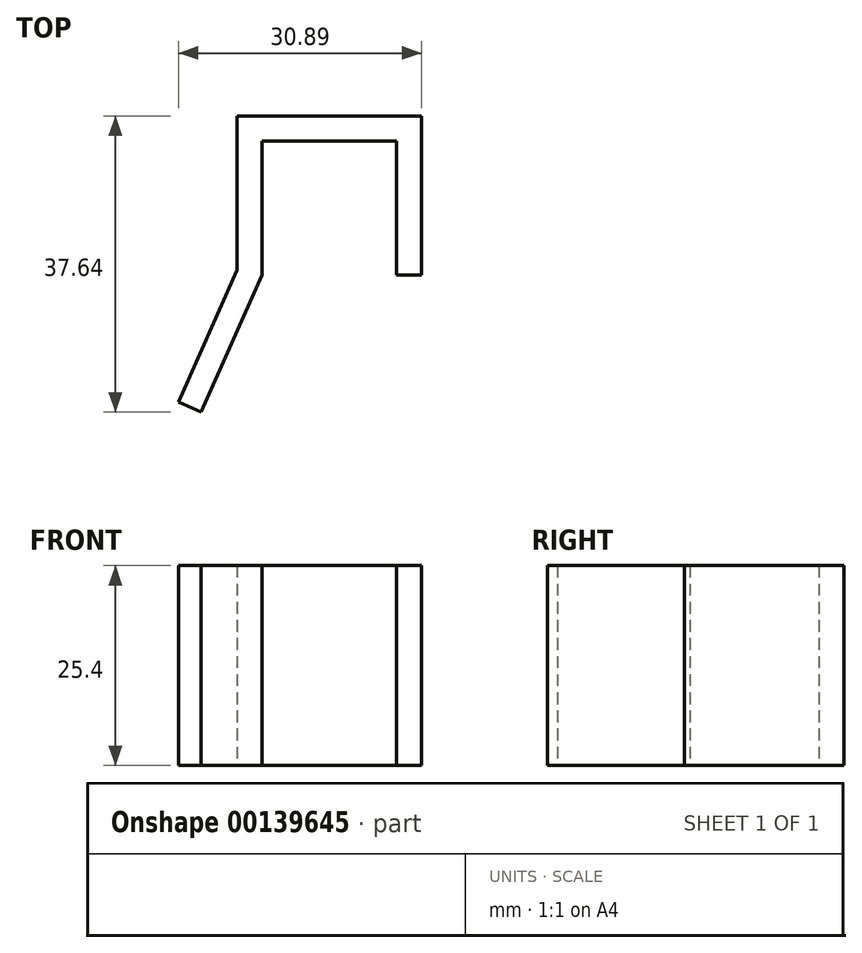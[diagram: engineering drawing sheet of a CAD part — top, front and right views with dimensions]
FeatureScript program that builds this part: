
annotation { "Feature Type Name" : "Feature", "Feature Type Description" : "" }
export const myFeature = defineFeature(function(context is Context, id is Id, definition is map)
    precondition{}
    {
        {
            var Q0;
            Q0=qCreatedBy(makeId("Top.planeOp"),FACE);
            var sketch = newSketch(context, id + "F0", { "sketchPlane" : qUnion([Q0])});
            skLineSegment(sketch, "E0.bottom", {"start": v(0, 0) * mm, "end": v(17.07, 0) * mm});
            skLineSegment(sketch, "E0.top", {"start": v(0, 17.07) * mm, "end": v(17.07, 17.07) * mm});
            skLineSegment(sketch, "E0.left", {"start": v(0, 0) * mm, "end": v(0, 17.07) * mm});
            skLineSegment(sketch, "E0.right", {"start": v(17.07, 0) * mm, "end": v(17.07, 17.07) * mm});
            skLineSegment(sketch, "E1", {"start": v(20.24, 0) * mm, "end": v(20.24, 20.24) * mm});
            skLineSegment(sketch, "E2", {"start": v(20.24, 20.24) * mm, "end": v(-3.18, 20.24) * mm});
            skLineSegment(sketch, "E3", {"start": v(-3.18, 20.24) * mm, "end": v(-3.17, 0.68) * mm});
            skLineSegment(sketch, "E4", {"start": v(17.07, 0) * mm, "end": v(17.07, 0) * mm});
            skLineSegment(sketch, "E5", {"start": v(17.07, 0) * mm, "end": v(20.24, 0) * mm});
            skLineSegment(sketch, "E6", {"start": v(0, 0) * mm, "end": v(-7.75, -17.4) * mm});
            skLineSegment(sketch, "E7", {"start": v(-7.75, -17.4) * mm, "end": v(-10.65, -16.1) * mm});
            skLineSegment(sketch, "E8", {"start": v(-10.65, -16.1) * mm, "end": v(-3.17, 0.68) * mm});
            skSolve(sketch);
        }
        {
            var Q0;
            Q0=makeQuery(id+"F0.imprint","IMPRINT",FACE,{"disambiguationData":[TD([[makeQuery(id+"F0.imprint","IMPRINT",EDGE,{"derivedFrom":sQuery(id+"F0.wireOp",EDGE,"E0.top")}),1.0]])]});
            extrude(context, id + "F1", {"entities" : qUnion([Q0]), "depth" : 25.4 * mm});
        }
    });
